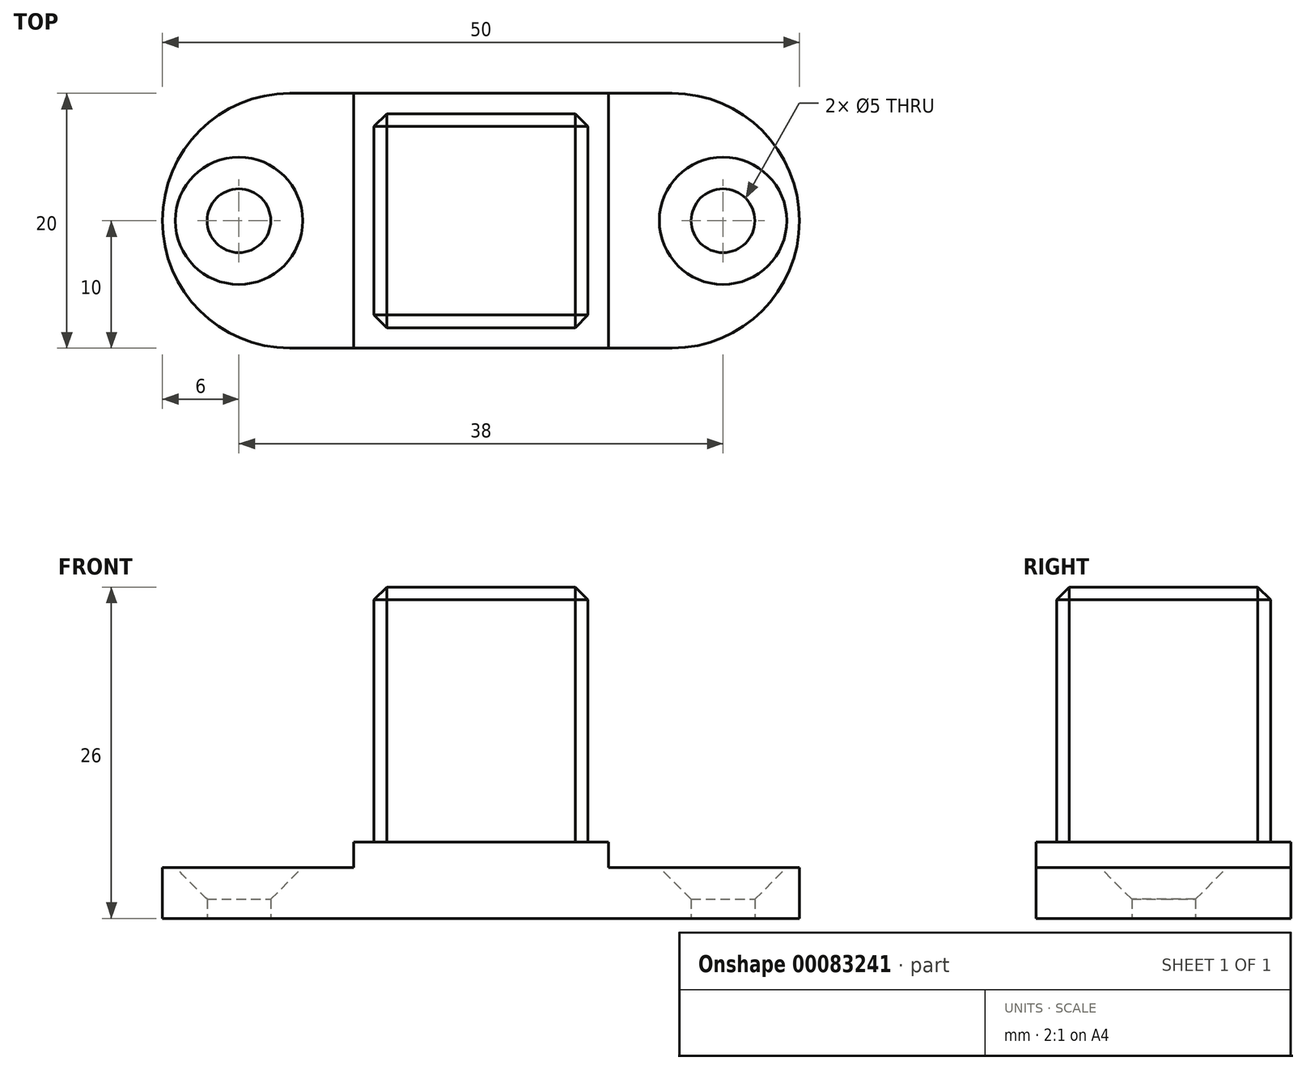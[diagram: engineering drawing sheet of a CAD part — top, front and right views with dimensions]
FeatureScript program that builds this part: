
annotation { "Feature Type Name" : "Feature", "Feature Type Description" : "" }
export const myFeature = defineFeature(function(context is Context, id is Id, definition is map)
    precondition{}
    {
        {
            var Q0;
            Q0=qCreatedBy(makeId("Top.planeOp"),FACE);
            var sketch = newSketch(context, id + "F0", { "sketchPlane" : qUnion([Q0])});
            skLineSegment(sketch, "E0.bottom", {"start": v(0, 0) * mm, "end": v(30, 0) * mm});
            skLineSegment(sketch, "E0.top", {"start": v(0, 20) * mm, "end": v(30, 20) * mm});
            skLineSegment(sketch, "E0.left", {"start": v(0, 0) * mm, "end": v(0, 20) * mm});
            skLineSegment(sketch, "E0.right", {"start": v(30, 0) * mm, "end": v(30, 20) * mm});
            skArc(sketch, "E1", {"start": v(0, 20) * mm, "mid": v(-10, 10) * mm, "end": v(0, 0) * mm});
            skArc(sketch, "E2", {"start": v(30, 0) * mm, "mid": v(40, 10) * mm, "end": v(30, 20) * mm});
            skLineSegment(sketch, "E3", {"start": v(5, 20) * mm, "end": v(5, 0) * mm});
            skLineSegment(sketch, "E4", {"start": v(25, 20) * mm, "end": v(25, 0) * mm});
            skPoint(sketch, "E5", {"position": v(-4, 10) * mm});
            skPoint(sketch, "E6", {"position": v(34, 10) * mm});
            skSolve(sketch);
        }
        {
            var Q0;
            {var subQ1=sQuery(id+"F0.wireOp",EDGE,"E3");Q0=makeQuery(id+"F0.imprint","IMPRINT",FACE,{"disambiguationData":[TD([[makeQuery(id+"F0.imprint","IMPRINT",EDGE,{"derivedFrom":subQ1}),1.0]])]});}
            extrude(context, id + "F1", {"entities" : qUnion([Q0]), "depth" : 2 * mm});
        }
        {
            var Q0;
            Q0=qSketchRegion(id+"F0",true);
            extrude(context, id + "F2", {"entities" : qUnion([Q0]), "operationType" : NewBodyOperationType.ADD, "oppositeDirection" : true, "depth" : 4 * mm});
        }
        {
            var Q0;
            Q0=makeQuery(id+"F1.opExtrude","CAP_FACE",FACE,{"disambiguationData":[OSD([sQuery(id+"F0.wireOp",EDGE,"E0.bottom"),sQuery(id+"F0.wireOp",EDGE,"E0.top"),sQuery(id+"F0.wireOp",EDGE,"E3"),sQuery(id+"F0.wireOp",EDGE,"E4")])],"isStart":false});
            var sketch = newSketch(context, id + "F3", { "sketchPlane" : qUnion([Q0])});
            skLineSegment(sketch, "E7", {"start": v(6.6, 18.4) * mm, "end": v(23.4, 18.4) * mm});
            skLineSegment(sketch, "E8", {"start": v(23.4, 18.4) * mm, "end": v(23.4, 1.6) * mm});
            skLineSegment(sketch, "E9", {"start": v(6.6, 18.4) * mm, "end": v(6.6, 1.6) * mm});
            skLineSegment(sketch, "E10", {"start": v(6.6, 1.6) * mm, "end": v(23.4, 1.6) * mm});
            skSolve(sketch);
        }
        {
            var Q0;
            Q0=makeQuery(id+"F3.imprint","IMPRINT",FACE,{"disambiguationData":[TD([[makeQuery(id+"F3.imprint","IMPRINT",EDGE,{"derivedFrom":sQuery(id+"F3.wireOp",EDGE,"E7")}),-1.0]])]});
            extrude(context, id + "F4", {"entities" : qUnion([Q0]), "operationType" : NewBodyOperationType.ADD, "depth" : 20 * mm});
        }
        {
            var Q0;
            Q0=makeQuery(id+"F4.opExtrude","SWEPT_EDGE",EDGE,{"disambiguationData":[OSD([sQuery(id+"F3.wireOp",EDGE,"E7"),sQuery(id+"F3.wireOp",EDGE,"E8")])]});
            var Q1;
            Q1=makeQuery(id+"F4.opExtrude","SWEPT_EDGE",EDGE,{"disambiguationData":[OSD([sQuery(id+"F3.wireOp",EDGE,"E7"),sQuery(id+"F3.wireOp",EDGE,"E9")])]});
            var Q2;
            Q2=makeQuery(id+"F4.opExtrude","CAP_EDGE",EDGE,{"disambiguationData":[OSD([sQuery(id+"F3.wireOp",EDGE,"E7")])],"isStart":false});
            var Q3;
            Q3=makeQuery(id+"F4.opExtrude","CAP_EDGE",EDGE,{"disambiguationData":[OSD([sQuery(id+"F3.wireOp",EDGE,"E9")])],"isStart":false});
            var Q4;
            Q4=makeQuery(id+"F4.opExtrude","CAP_EDGE",EDGE,{"disambiguationData":[OSD([sQuery(id+"F3.wireOp",EDGE,"E8")])],"isStart":false});
            var Q5;
            Q5=makeQuery(id+"F4.opExtrude","CAP_EDGE",EDGE,{"disambiguationData":[OSD([sQuery(id+"F3.wireOp",EDGE,"E10")])],"isStart":false});
            var Q6;
            Q6=makeQuery(id+"F4.opExtrude","SWEPT_EDGE",EDGE,{"disambiguationData":[OSD([sQuery(id+"F3.wireOp",EDGE,"E8"),sQuery(id+"F3.wireOp",EDGE,"E10")])]});
            var Q7;
            Q7=makeQuery(id+"F4.opExtrude","SWEPT_EDGE",EDGE,{"disambiguationData":[OSD([sQuery(id+"F3.wireOp",EDGE,"E9"),sQuery(id+"F3.wireOp",EDGE,"E10")])]});
            chamfer(context, id + "F5", {"entities" : qUnion([Q0, Q1, Q2, Q3, Q4, Q5, Q6, Q7]), "width" : 1 * mm, "tangentPropagation" : true});
        }
        {
            var Q0;
            Q0=sQuery(id+"F0.wireOp",VERTEX,"E5");
            var Q1;
            Q1=sQuery(id+"F0.wireOp",VERTEX,"E6");
            var Q2;
            Q2=makeQuery(id+"F1.opExtrude","SWEPT_BODY",BODY,{"disambiguationData":[OSD([sQuery(id+"F0.wireOp",EDGE,"E0.bottom"),sQuery(id+"F0.wireOp",EDGE,"E0.top"),sQuery(id+"F0.wireOp",EDGE,"E3"),sQuery(id+"F0.wireOp",EDGE,"E4")])]});
            hole(context, id + "F6", {"style" : HoleStyle.C_SINK, "endStyle" : HoleEndStyle.THROUGH, "holeDiameter" : 5 * mm, "cSinkDiameter" : 10 * mm, "cSinkAngle" : 90 * degree, "locations" : qUnion([Q0, Q1]), "scope" : qUnion([Q2]), "isTappedThrough" : true, "startStyle" : HoleStartStyle.PART});
        }
    });
